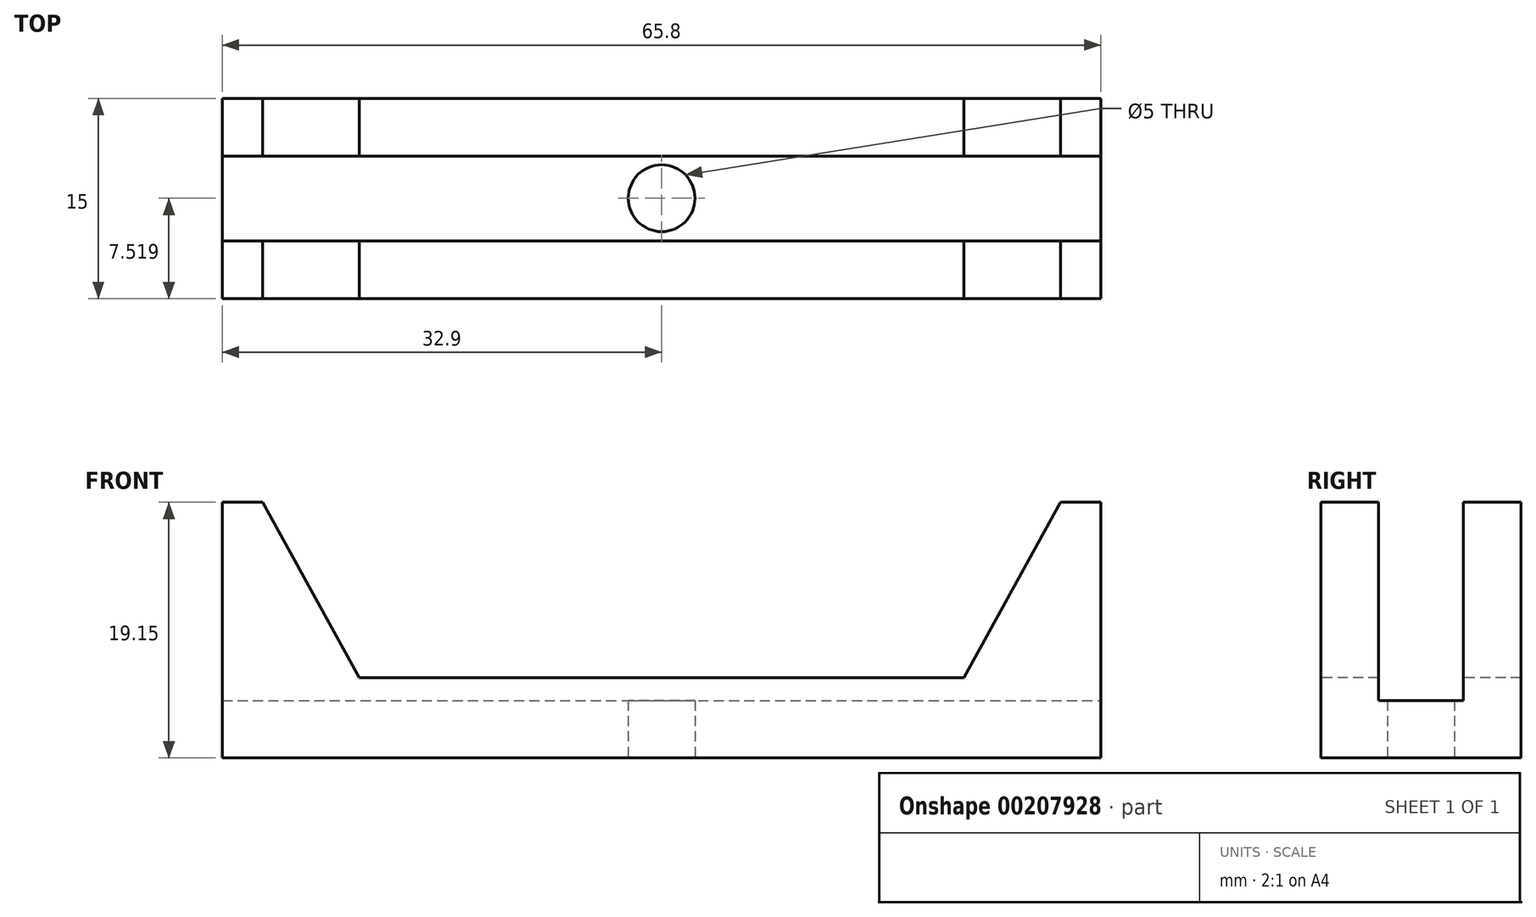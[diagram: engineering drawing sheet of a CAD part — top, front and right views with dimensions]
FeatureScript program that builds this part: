
annotation { "Feature Type Name" : "Feature", "Feature Type Description" : "" }
export const myFeature = defineFeature(function(context is Context, id is Id, definition is map)
    precondition{}
    {
        {
            var Q0;
            Q0=qCreatedBy(makeId("Top.planeOp"),FACE);
            var sketch = newSketch(context, id + "F0", { "sketchPlane" : qUnion([Q0])});
            skLineSegment(sketch, "E0.top", {"start": v(-30, -4.24) * mm, "end": v(30, -4.24) * mm});
            skPoint(sketch, "E0.middle", {"position": v(0, 0) * mm});
            skLineSegment(sketch, "E1.bottom", {"start": v(-35.1, 7.41) * mm, "end": v(-28.57, 7.41) * mm});
            skLineSegment(sketch, "E1.right", {"start": v(32.9, 7.41) * mm, "end": v(32.9, 1.06) * mm});
            skPoint(sketch, "E1.middle", {"position": v(-1.1, 4.24) * mm});
            skLineSegment(sketch, "E2.MirrorCS", {"start": v(35.1, 7.41) * mm, "end": v(28.57, 7.41) * mm});
            skLineSegment(sketch, "E3.trimOffspring", {"start": v(28.57, 7.41) * mm, "end": v(32.9, 7.41) * mm});
            skLineSegment(sketch, "E4.trimOffspring", {"start": v(-28.57, 7.41) * mm, "end": v(-32.9, 7.41) * mm});
            skLineSegment(sketch, "E5", {"start": v(-28.85, 9.05) * mm, "end": v(-28.79, 7.41) * mm});
            skLineSegment(sketch, "E6.MirrorCS", {"start": v(28.85, 9.05) * mm, "end": v(28.79, 7.41) * mm});
            skPoint(sketch, "E7.orphan", {"position": v(-21.32, -4.24) * mm});
            skPoint(sketch, "E8.orphan", {"position": v(23.52, -4.24) * mm});
            skLineSegment(sketch, "E9", {"start": v(-28.57, 7.41) * mm, "end": v(28.57, 7.41) * mm});
            skPoint(sketch, "E10.MirrorCS.start.orphan", {"position": v(23.52, 4.24) * mm});
            skPoint(sketch, "E11.orphan", {"position": v(21.32, 4.24) * mm});
            skPoint(sketch, "E0.bottom.start.orphan", {"position": v(-23.52, 4.24) * mm});
            skLineSegment(sketch, "E12", {"start": v(-32.9, 7.41) * mm, "end": v(-32.9, 1.06) * mm});
            skPoint(sketch, "E1.top.end.orphan", {"position": v(-28.57, 1.72) * mm});
            skPoint(sketch, "E13.trimOffspring.start.orphan", {"position": v(-35.1, 1.06) * mm});
            skPoint(sketch, "E14.MirrorCS.end.orphan", {"position": v(28.57, 1.72) * mm});
            skPoint(sketch, "E15.trimOffspring.start.orphan", {"position": v(35.1, 1.06) * mm});
            skLineSegment(sketch, "E16.top", {"start": v(-32.9, -4.24) * mm, "end": v(-30, -4.24) * mm});
            skLineSegment(sketch, "E16.left", {"start": v(-32.9, 1.06) * mm, "end": v(-32.9, -4.24) * mm});
            skLineSegment(sketch, "E17.top", {"start": v(32.9, -4.24) * mm, "end": v(30, -4.24) * mm});
            skLineSegment(sketch, "E17.left", {"start": v(32.9, 1.06) * mm, "end": v(32.9, -4.24) * mm});
            skSolve(sketch);
        }
        {
            var Q0;
            Q0=makeQuery(id+"F0.imprint","IMPRINT",FACE,{"disambiguationData":[TD([[makeQuery(id+"F0.imprint","IMPRINT",EDGE,{"derivedFrom":sQuery(id+"F0.wireOp",EDGE,"E0.bottom")}),-1.0]])]});
            var Q1;
            Q1=makeQuery(id+"F0.imprint","IMPRINT",FACE,{"disambiguationData":[TD([[makeQuery(id+"F0.imprint","IMPRINT",EDGE,{"derivedFrom":sQuery(id+"F0.wireOp",EDGE,"E0.top")}),1.0]])]});
            extrude(context, id + "F1", {"entities" : qUnion([Q0, Q1]), "depth" : 15 * mm});
        }
        {
            var Q0;
            Q0=makeQuery(id+"F1.opExtrude","SWEPT_FACE",FACE,{"disambiguationData":[OSD([sQuery(id+"F0.wireOp",EDGE,"E0.top")])]});
            var sketch = newSketch(context, id + "F2", { "sketchPlane" : qUnion([Q0])});
            skCircle(sketch, "E18", {"center": v(0, 7.48) * mm, "radius": 2.5 * mm});
            skCircle(sketch, "E19", {"center": v(0, 7.48) * mm, "radius": 5.98 * mm});
            skSolve(sketch);
        }
        {
            var Q0;
            Q0=makeQuery(id+"F2.imprint","IMPRINT",FACE,{"disambiguationData":[TD([[makeQuery(id+"F2.imprint","IMPRINT",EDGE,{"derivedFrom":sQuery(id+"F2.wireOp",EDGE,"E18")}),1.0]])]});
            extrude(context, id + "F3", {"entities" : qUnion([Q0]), "operationType" : NewBodyOperationType.REMOVE, "endBound" : BoundingType.THROUGH_ALL, "oppositeDirection" : true, "depth" : 25 * mm});
        }
        {
            var Q0;
            {var subQ0=sQuery(id+"F0.wireOp",EDGE,"E9");var subQ7=sQuery(id+"F0.wireOp",EDGE,"E3.trimOffspring");var subQ8=sQuery(id+"F0.wireOp",EDGE,"E4.trimOffspring");var subQ9=sQuery(id+"F0.wireOp",EDGE,"E1.right");Q0=makeQuery(id+"FR2D4R5otbcXBe0_1.boolean.opBoolean","SPLIT",FACE,{"disambiguationData":[TD([makeQuery(id+"F1.opExtrude","SWEPT_FACE",FACE,{"disambiguationData":[OSD([subQ9])]})])],"derivedFrom":makeQuery(id+"F1.opExtrude","SWEPT_FACE",FACE,{"disambiguationData":[OSD([subQ8,subQ7,subQ0])]})});}
            var Q1;
            {var subQ0=sQuery(id+"F0.wireOp",EDGE,"E9");var subQ7=sQuery(id+"F0.wireOp",EDGE,"E3.trimOffspring");var subQ8=sQuery(id+"F0.wireOp",EDGE,"E4.trimOffspring");var subQ10=sQuery(id+"F0.wireOp",EDGE,"E1.left");Q1=makeQuery(id+"FR2D4R5otbcXBe0_1.boolean.opBoolean","SPLIT",FACE,{"disambiguationData":[TD([makeQuery(id+"F1.opExtrude","SWEPT_FACE",FACE,{"disambiguationData":[OSD([subQ10])]})])],"derivedFrom":makeQuery(id+"F1.opExtrude","SWEPT_FACE",FACE,{"disambiguationData":[OSD([subQ8,subQ7,subQ0])]})});}
            extrude(context, id + "F4", {"entities" : qUnion([Q0, Q1]), "operationType" : NewBodyOperationType.ADD, "depth" : 5 * mm});
        }
        {
            var Q0;
            {var subQ0=sQuery(id+"F0.wireOp",EDGE,"E3.trimOffspring");var subQ1=sQuery(id+"F0.wireOp",EDGE,"E1.right");Q0=makeQuery(id+"F4.boolean.opBoolean","MERGE",FACE,{"derivedFrom":[makeQuery(id+"F1.opExtrude","SWEPT_FACE",FACE,{"disambiguationData":[OSD([subQ1])]}),makeQuery(id+"F4.opExtrude","SWEPT_FACE",FACE,{"disambiguationData":[OSD([subQ1,subQ0]),TDD([makeQuery(id+"F1.opExtrude","SWEPT_EDGE",EDGE,{"disambiguationData":[OSD([subQ1,subQ0])]})])]})]});}
            var sketch = newSketch(context, id + "F5", { "sketchPlane" : qUnion([Q0])});
            skLineSegment(sketch, "E20.bottom", {"start": v(6.06, 10.67) * mm, "end": v(12.41, 10.67) * mm});
            skLineSegment(sketch, "E20.top", {"start": v(6.06, 4.33) * mm, "end": v(12.41, 4.33) * mm});
            skLineSegment(sketch, "E20.left", {"start": v(6.06, 10.67) * mm, "end": v(6.06, 4.32) * mm});
            skPoint(sketch, "E20.middle", {"position": v(12.41, 7.5) * mm});
            skPoint(sketch, "E21", {"position": v(12.41, 10.67) * mm});
            skPoint(sketch, "E22", {"position": v(12.41, 4.33) * mm});
            skPoint(sketch, "E20.right.start.orphan", {"position": v(18.76, 10.68) * mm});
            skPoint(sketch, "E23.orphan", {"position": v(18.76, 4.33) * mm});
            skSolve(sketch);
        }
        {
            var Q0;
            {var subQ0=sQuery(id+"F5.wireOp",EDGE,"E20.bottom");Q0=makeQuery(id+"F5.imprint","IMPRINT",FACE,{"disambiguationData":[TD([[makeQuery(id+"F5.imprint","IMPRINT",EDGE,{"derivedFrom":subQ0}),-1.0]])]});}
            extrude(context, id + "F6", {"entities" : qUnion([Q0]), "operationType" : NewBodyOperationType.REMOVE, "endBound" : BoundingType.THROUGH_ALL, "oppositeDirection" : true, "depth" : 25 * mm});
        }
        {
            var Q0;
            Q0=makeQuery(id+"F1.opExtrude","SWEPT_BODY",BODY,{"disambiguationData":[OSD([sQuery(id+"F0.wireOp",EDGE,"E0.top"),sQuery(id+"F0.wireOp",EDGE,"E1.left"),sQuery(id+"F0.wireOp",EDGE,"E1.right"),sQuery(id+"F0.wireOp",EDGE,"E4.trimOffspring"),sQuery(id+"F0.wireOp",EDGE,"E3.trimOffspring"),sQuery(id+"F0.wireOp",EDGE,"E13.trimOffspring"),sQuery(id+"F0.wireOp",EDGE,"E15.trimOffspring"),sQuery(id+"F0.wireOp",EDGE,"E5"),sQuery(id+"F0.wireOp",EDGE,"E6.MirrorCS"),sQuery(id+"F0.wireOp",EDGE,"E9")])]});
            var Q1;
            {var subQ0=sQuery(id+"F0.wireOp",EDGE,"E9");var subQ1=sQuery(id+"F0.wireOp",EDGE,"E3.trimOffspring");var subQ2=sQuery(id+"F0.wireOp",EDGE,"E4.trimOffspring");Q1=makeQuery(id+"F4.opExtrude","CAP_EDGE",EDGE,{"disambiguationData":[OSD([subQ2,subQ1,subQ0]),TDD([makeQuery(id+"F1.opExtrude","CAP_EDGE",EDGE,{"disambiguationData":[OSD([subQ2,subQ1,subQ0])],"isStart":true})])],"isStart":false});}
            var Q2;
            {var subQ0=sQuery(id+"F0.wireOp",EDGE,"E9");var subQ1=sQuery(id+"F0.wireOp",EDGE,"E3.trimOffspring");var subQ2=sQuery(id+"F0.wireOp",EDGE,"E4.trimOffspring");Q2=makeQuery(id+"F4.opExtrude","CAP_EDGE",EDGE,{"disambiguationData":[OSD([subQ2,subQ1,subQ0]),TDD([makeQuery(id+"F1.opExtrude","CAP_EDGE",EDGE,{"disambiguationData":[OSD([subQ2,subQ1,subQ0])],"isStart":true})])],"isStart":false});}
            transform(context, id + "F7", {"entities" : qUnion([Q0]), "transformType" : TransformType.ROTATION, "transformAxis" : qUnion([Q2]), "angle" : 90 * degree, "makeCopy" : false});
        }
        {
            var Q0;
            Q0=makeQuery(id+"F6.boolean.opBoolean","COPY",FACE,{"derivedFrom":makeQuery(id+"F6.opExtrude","SWEPT_FACE",FACE,{"disambiguationData":[OSD([sQuery(id+"F5.wireOp",EDGE,"E20.left")])]})});
            extrude(context, id + "F8", {"entities" : qUnion([Q0]), "operationType" : NewBodyOperationType.REMOVE, "oppositeDirection" : true, "depth" : 4 * mm});
        }
        {
            var Q0;
            Q0=makeQuery(id+"F1.opExtrude","SWEPT_FACE",FACE,{"disambiguationData":[OSD([sQuery(id+"F0.wireOp",EDGE,"E0.top"),sQuery(id+"F0.wireOp",EDGE,"E16.top"),sQuery(id+"F0.wireOp",EDGE,"E17.top")])]});
            extrude(context, id + "F9", {"entities" : qUnion([Q0]), "operationType" : NewBodyOperationType.ADD, "depth" : 6 * mm});
        }
        {
            var Q0;
            {var subQ4=sQuery(id+"F0.wireOp",EDGE,"E3.trimOffspring");var subQ5=sQuery(id+"F0.wireOp",EDGE,"E9");var subQ6=sQuery(id+"F0.wireOp",EDGE,"E4.trimOffspring");Q0=makeQuery(id+"F6.boolean.opBoolean","SPLIT",FACE,{"disambiguationData":[TD([makeQuery(id+"F6.opExtrude","SWEPT_FACE",FACE,{"disambiguationData":[OSD([sQuery(id+"F5.wireOp",EDGE,"E20.top")])]})])],"derivedFrom":makeQuery(id+"F4.opExtrude","CAP_FACE",FACE,{"disambiguationData":[OSD([subQ6,subQ4,subQ5])],"isStart":false})});}
            var Q1;
            {var subQ4=sQuery(id+"F0.wireOp",EDGE,"E3.trimOffspring");var subQ5=sQuery(id+"F0.wireOp",EDGE,"E9");var subQ6=sQuery(id+"F0.wireOp",EDGE,"E4.trimOffspring");Q1=makeQuery(id+"F6.boolean.opBoolean","SPLIT",FACE,{"disambiguationData":[TD([makeQuery(id+"F6.opExtrude","SWEPT_FACE",FACE,{"disambiguationData":[OSD([sQuery(id+"F5.wireOp",EDGE,"E20.bottom")])]})])],"derivedFrom":makeQuery(id+"F4.opExtrude","CAP_FACE",FACE,{"disambiguationData":[OSD([subQ6,subQ4,subQ5])],"isStart":false})});}
            extrude(context, id + "F10", {"entities" : qUnion([Q0, Q1]), "operationType" : NewBodyOperationType.REMOVE, "oppositeDirection" : true, "depth" : 3.5 * mm});
        }
        {
            var Q0;
            Q0=makeQuery(id+"F8.boolean.opBoolean","COPY",FACE,{"derivedFrom":makeQuery(id+"F8.opExtrude","CAP_FACE",FACE,{"disambiguationData":[OSD([sQuery(id+"F5.wireOp",EDGE,"E20.left")])],"isStart":false})});
            extrude(context, id + "F11", {"entities" : qUnion([Q0]), "operationType" : NewBodyOperationType.REMOVE, "oppositeDirection" : true, "depth" : 8 * mm});
        }
        {
            var Q0;
            {var subQ0=sQuery(id+"F0.wireOp",EDGE,"E17.top");var subQ1=sQuery(id+"F0.wireOp",EDGE,"E16.top");var subQ2=sQuery(id+"F0.wireOp",EDGE,"E0.top");var subQ3=sQuery(id+"F0.wireOp",EDGE,"E9");var subQ4=sQuery(id+"F0.wireOp",EDGE,"E3.trimOffspring");var subQ5=sQuery(id+"F0.wireOp",EDGE,"E4.trimOffspring");Q0=makeQuery(id+"F9.boolean.opBoolean","MERGE",FACE,{"derivedFrom":[makeQuery(id+"F4.boolean.opBoolean","MERGE",FACE,{"derivedFrom":[makeQuery(id+"F1.opExtrude","CAP_FACE",FACE,{"disambiguationData":[OSD([subQ2,sQuery(id+"F0.wireOp",EDGE,"E1.right"),subQ5,subQ4,subQ3,sQuery(id+"F0.wireOp",EDGE,"E12"),subQ1,sQuery(id+"F0.wireOp",EDGE,"E16.left"),subQ0,sQuery(id+"F0.wireOp",EDGE,"E17.left")])],"isStart":true}),makeQuery(id+"F4.opExtrude","SWEPT_FACE",FACE,{"disambiguationData":[OSD([subQ5,subQ4,subQ3]),TDD([makeQuery(id+"F1.opExtrude","CAP_EDGE",EDGE,{"disambiguationData":[OSD([subQ5,subQ4,subQ3])],"isStart":true})])]})]}),makeQuery(id+"F9.opExtrude","SWEPT_FACE",FACE,{"disambiguationData":[OSD([subQ2,subQ1,subQ0]),TDD([makeQuery(id+"F1.opExtrude","CAP_EDGE",EDGE,{"disambiguationData":[OSD([subQ2,subQ1,subQ0])],"isStart":true})])]})]});}
            var sketch = newSketch(context, id + "F12", { "sketchPlane" : qUnion([Q0])});
            skLineSegment(sketch, "E24.bottom", {"start": v(32.87, -16.65) * mm, "end": v(-32.87, -16.65) * mm});
            skLineSegment(sketch, "E24.top", {"start": v(32.87, 9.65) * mm, "end": v(-32.87, 9.65) * mm});
            skLineSegment(sketch, "E24.left", {"start": v(32.87, -16.65) * mm, "end": v(32.87, 9.65) * mm});
            skLineSegment(sketch, "E24.right", {"start": v(-32.87, -16.65) * mm, "end": v(-32.87, 9.65) * mm});
            skPoint(sketch, "E24.middle", {"position": v(0, -3.5) * mm});
            skSolve(sketch);
        }
        {
            var Q0;
            {var subQ0=sQuery(id+"F12.wireOp",EDGE,"E24.bottom");Q0=makeQuery(id+"F12.imprint","IMPRINT",FACE,{"disambiguationData":[TD([[makeQuery(id+"F12.imprint","IMPRINT",EDGE,{"derivedFrom":subQ0}),-1.0]])]});}
            extrude(context, id + "F13", {"entities" : qUnion([Q0]), "operationType" : NewBodyOperationType.REMOVE, "oppositeDirection" : true, "depth" : 25 * mm});
        }
        {
            var Q0;
            {var subQ0=sQuery(id+"F0.wireOp",EDGE,"E17.top");var subQ1=sQuery(id+"F0.wireOp",EDGE,"E16.top");var subQ2=sQuery(id+"F0.wireOp",EDGE,"E0.top");var subQ3=sQuery(id+"F0.wireOp",EDGE,"E9");var subQ4=sQuery(id+"F0.wireOp",EDGE,"E3.trimOffspring");var subQ5=sQuery(id+"F0.wireOp",EDGE,"E4.trimOffspring");Q0=makeQuery(id+"F9.boolean.opBoolean","MERGE",FACE,{"derivedFrom":[makeQuery(id+"F4.boolean.opBoolean","MERGE",FACE,{"derivedFrom":[makeQuery(id+"F1.opExtrude","CAP_FACE",FACE,{"disambiguationData":[OSD([subQ2,sQuery(id+"F0.wireOp",EDGE,"E1.right"),subQ5,subQ4,subQ3,sQuery(id+"F0.wireOp",EDGE,"E12"),subQ1,sQuery(id+"F0.wireOp",EDGE,"E16.left"),subQ0,sQuery(id+"F0.wireOp",EDGE,"E17.left")])],"isStart":false}),makeQuery(id+"F4.opExtrude","SWEPT_FACE",FACE,{"disambiguationData":[OSD([subQ5,subQ4,subQ3]),TDD([makeQuery(id+"F1.opExtrude","CAP_EDGE",EDGE,{"disambiguationData":[OSD([subQ5,subQ4,subQ3])],"isStart":false})])]})]}),makeQuery(id+"F9.opExtrude","SWEPT_FACE",FACE,{"disambiguationData":[OSD([subQ2,subQ1,subQ0]),TDD([makeQuery(id+"F1.opExtrude","CAP_EDGE",EDGE,{"disambiguationData":[OSD([subQ2,subQ1,subQ0])],"isStart":false})])]})]});}
            var sketch = newSketch(context, id + "F14", { "sketchPlane" : qUnion([Q0])});
            skLineSegment(sketch, "E25", {"start": v(-32.87, -3.5) * mm, "end": v(-29.87, -3.5) * mm});
            skLineSegment(sketch, "E26", {"start": v(-29.87, -3.5) * mm, "end": v(-22.64, -16.65) * mm});
            skLineSegment(sketch, "E27.MirrorCS", {"start": v(29.87, -3.5) * mm, "end": v(22.64, -16.65) * mm});
            skLineSegment(sketch, "E28.MirrorCS", {"start": v(32.87, -3.5) * mm, "end": v(29.87, -3.5) * mm});
            skSolve(sketch);
        }
        {
            var Q0;
            {var subQ0=sQuery(id+"F14.wireOp",EDGE,"E27.MirrorCS");Q0=makeQuery(id+"F14.imprint","IMPRINT",FACE,{"disambiguationData":[TD([[makeQuery(id+"F14.imprint","IMPRINT",EDGE,{"derivedFrom":subQ0}),1.0]])]});}
            var Q1;
            Q1=makeQuery(id+"F14.imprint","IMPRINT",FACE,{"disambiguationData":[TD([[makeQuery(id+"F14.imprint","IMPRINT",EDGE,{"derivedFrom":sQuery(id+"F14.wireOp",EDGE,"E25")}),-1.0]])]});
            var Q2;
            {var subQ0=sQuery(id+"F0.wireOp",EDGE,"E17.top");var subQ1=sQuery(id+"F0.wireOp",EDGE,"E16.top");var subQ2=sQuery(id+"F0.wireOp",EDGE,"E0.top");var subQ3=sQuery(id+"F0.wireOp",EDGE,"E9");var subQ4=sQuery(id+"F0.wireOp",EDGE,"E3.trimOffspring");var subQ5=sQuery(id+"F0.wireOp",EDGE,"E4.trimOffspring");Q2=makeQuery(id+"F9.boolean.opBoolean","MERGE",FACE,{"derivedFrom":[makeQuery(id+"F4.boolean.opBoolean","MERGE",FACE,{"derivedFrom":[makeQuery(id+"F1.opExtrude","CAP_FACE",FACE,{"disambiguationData":[OSD([subQ2,sQuery(id+"F0.wireOp",EDGE,"E1.right"),subQ5,subQ4,subQ3,sQuery(id+"F0.wireOp",EDGE,"E12"),subQ1,sQuery(id+"F0.wireOp",EDGE,"E16.left"),subQ0,sQuery(id+"F0.wireOp",EDGE,"E17.left")])],"isStart":true}),makeQuery(id+"F4.opExtrude","SWEPT_FACE",FACE,{"disambiguationData":[OSD([subQ5,subQ4,subQ3]),TDD([makeQuery(id+"F1.opExtrude","CAP_EDGE",EDGE,{"disambiguationData":[OSD([subQ5,subQ4,subQ3])],"isStart":true})])]})]}),makeQuery(id+"F9.opExtrude","SWEPT_FACE",FACE,{"disambiguationData":[OSD([subQ2,subQ1,subQ0]),TDD([makeQuery(id+"F1.opExtrude","CAP_EDGE",EDGE,{"disambiguationData":[OSD([subQ2,subQ1,subQ0])],"isStart":true})])]})]});}
            extrude(context, id + "F15", {"entities" : qUnion([Q0, Q1]), "operationType" : NewBodyOperationType.ADD, "endBound" : BoundingType.UP_TO_SURFACE, "oppositeDirection" : true, "endBoundEntityFace" : qUnion([Q2]), "depth" : 19.7 * mm});
        }
        {
            var Q0;
            Q0=makeQuery(id+"F15.opExtrude","SWEPT_FACE",FACE,{"disambiguationData":[OSD([sQuery(id+"F0.wireOp",EDGE,"E0.top"),sQuery(id+"F0.wireOp",EDGE,"E1.right"),sQuery(id+"F0.wireOp",EDGE,"E4.trimOffspring"),sQuery(id+"F0.wireOp",EDGE,"E3.trimOffspring"),sQuery(id+"F0.wireOp",EDGE,"E9"),sQuery(id+"F0.wireOp",EDGE,"E12"),sQuery(id+"F0.wireOp",EDGE,"E16.top"),sQuery(id+"F0.wireOp",EDGE,"E16.left"),sQuery(id+"F0.wireOp",EDGE,"E17.top"),sQuery(id+"F0.wireOp",EDGE,"E17.left"),sQuery(id+"F12.wireOp",EDGE,"E24.left")])]});
            extrude(context, id + "F16", {"entities" : qUnion([Q0]), "operationType" : NewBodyOperationType.REMOVE, "endBound" : BoundingType.THROUGH_ALL, "oppositeDirection" : true, "depth" : 25 * mm});
        }
    });
